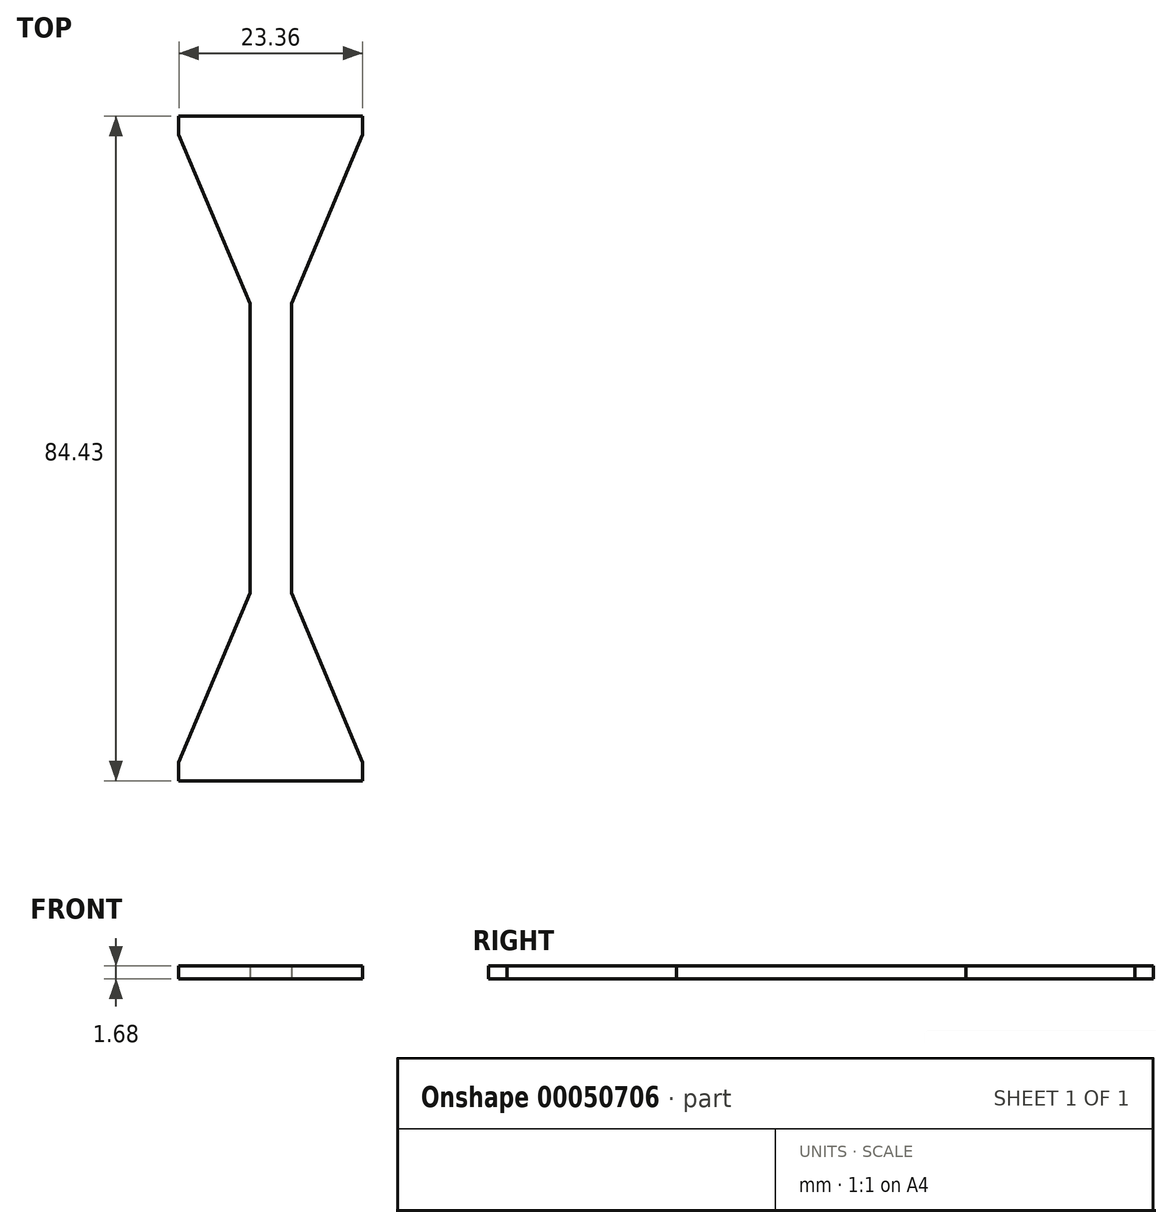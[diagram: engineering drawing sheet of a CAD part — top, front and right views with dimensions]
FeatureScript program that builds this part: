
annotation { "Feature Type Name" : "Feature", "Feature Type Description" : "" }
export const myFeature = defineFeature(function(context is Context, id is Id, definition is map)
    precondition{}
    {
        {
            var Q0;
            Q0=qCreatedBy(makeId("Top.planeOp"),FACE);
            var sketch = newSketch(context, id + "F0", { "sketchPlane" : qUnion([Q0])});
            skLineSegment(sketch, "E0", {"start": v(0, 17.54) * mm, "end": v(0, -19.34) * mm});
            skLineSegment(sketch, "E1", {"start": v(0, 17.54) * mm, "end": v(-2.65, 17.54) * mm});
            skLineSegment(sketch, "E2", {"start": v(0, 17.54) * mm, "end": v(2.65, 17.54) * mm});
            skLineSegment(sketch, "E3", {"start": v(-2.65, 17.54) * mm, "end": v(-2.65, -19.24) * mm});
            skLineSegment(sketch, "E4", {"start": v(2.65, 17.54) * mm, "end": v(2.65, -19.24) * mm});
            skLineSegment(sketch, "E5", {"start": v(2.65, -19.24) * mm, "end": v(-2.65, -19.24) * mm});
            skLineSegment(sketch, "E6", {"start": v(0, 17.54) * mm, "end": v(0, 41.32) * mm});
            skLineSegment(sketch, "E7", {"start": v(0, 41.32) * mm, "end": v(-11.68, 41.32) * mm});
            skLineSegment(sketch, "E8", {"start": v(0, 41.32) * mm, "end": v(11.68, 41.32) * mm});
            skLineSegment(sketch, "E9", {"start": v(0, -43.11) * mm, "end": v(-11.68, -43.11) * mm});
            skLineSegment(sketch, "E10", {"start": v(0, -43.11) * mm, "end": v(11.68, -43.11) * mm});
            skLineSegment(sketch, "E11", {"start": v(0, -19.34) * mm, "end": v(0, -43.11) * mm});
            skLineSegment(sketch, "E12", {"start": v(-11.68, 41.32) * mm, "end": v(-11.68, 38.98) * mm});
            skLineSegment(sketch, "E13", {"start": v(-11.68, 38.98) * mm, "end": v(-2.65, 17.54) * mm});
            skLineSegment(sketch, "E14", {"start": v(11.68, 41.32) * mm, "end": v(11.68, 38.98) * mm});
            skLineSegment(sketch, "E15", {"start": v(11.68, 38.98) * mm, "end": v(2.65, 17.54) * mm});
            skLineSegment(sketch, "E16", {"start": v(-11.68, -43.11) * mm, "end": v(-11.68, -40.77) * mm});
            skLineSegment(sketch, "E17", {"start": v(-11.68, -40.77) * mm, "end": v(-2.65, -19.24) * mm});
            skLineSegment(sketch, "E18", {"start": v(11.68, -43.11) * mm, "end": v(11.68, -40.77) * mm});
            skLineSegment(sketch, "E19", {"start": v(11.68, -40.77) * mm, "end": v(2.65, -19.24) * mm});
            skSolve(sketch);
        }
        {
            var Q0;
            Q0=makeQuery(id+"F0.imprint","IMPRINT",FACE,{"disambiguationData":[TD([[makeQuery(id+"F0.imprint","IMPRINT",EDGE,{"derivedFrom":sQuery(id+"F0.wireOp",EDGE,"E2")}),1.0]])]});
            var Q1;
            Q1=makeQuery(id+"F0.imprint","IMPRINT",FACE,{"disambiguationData":[TD([[makeQuery(id+"F0.imprint","IMPRINT",EDGE,{"derivedFrom":sQuery(id+"F0.wireOp",EDGE,"E1")}),-1.0]])]});
            var Q2;
            {var subQ0=sQuery(id+"F0.wireOp",EDGE,"E2");Q2=makeQuery(id+"F0.imprint","IMPRINT",FACE,{"disambiguationData":[TD([[makeQuery(id+"F0.imprint","IMPRINT",EDGE,{"derivedFrom":subQ0}),-1.0]])]});}
            var Q3;
            {var subQ0=sQuery(id+"F0.wireOp",EDGE,"E1");Q3=makeQuery(id+"F0.imprint","IMPRINT",FACE,{"disambiguationData":[TD([[makeQuery(id+"F0.imprint","IMPRINT",EDGE,{"derivedFrom":subQ0}),1.0]])]});}
            var Q4;
            Q4=makeQuery(id+"F0.imprint","IMPRINT",FACE,{"disambiguationData":[TD([[makeQuery(id+"F0.imprint","IMPRINT",EDGE,{"derivedFrom":sQuery(id+"F0.wireOp",EDGE,"E9")}),-1.0]])]});
            var Q5;
            Q5=makeQuery(id+"F0.imprint","IMPRINT",FACE,{"disambiguationData":[TD([[makeQuery(id+"F0.imprint","IMPRINT",EDGE,{"derivedFrom":sQuery(id+"F0.wireOp",EDGE,"E10")}),1.0]])]});
            extrude(context, id + "F1", {"entities" : qUnion([Q0, Q1, Q2, Q3, Q4, Q5]), "depth" : 1.68 * mm});
        }
    });
